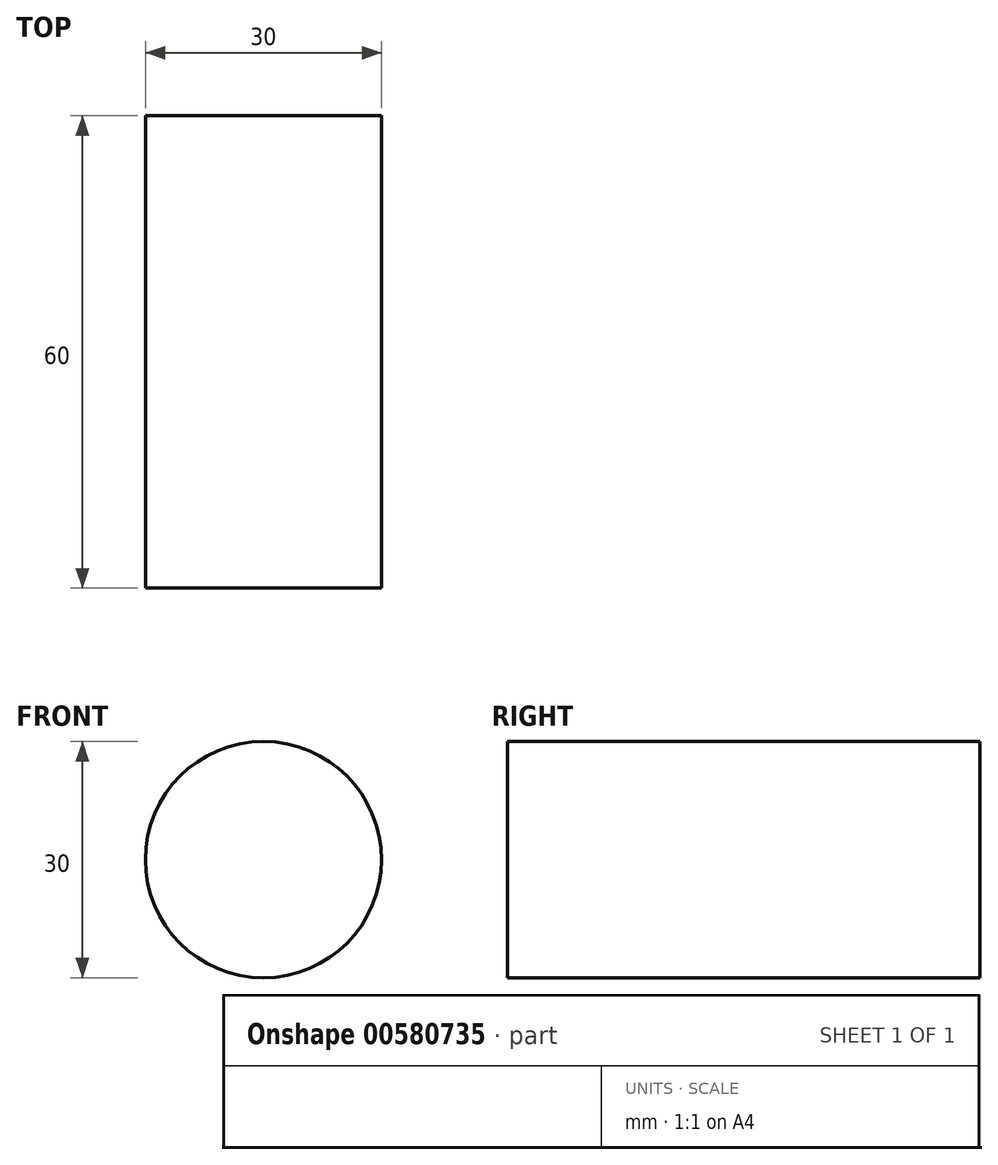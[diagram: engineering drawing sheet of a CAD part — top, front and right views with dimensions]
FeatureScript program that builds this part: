
annotation { "Feature Type Name" : "Feature", "Feature Type Description" : "" }
export const myFeature = defineFeature(function(context is Context, id is Id, definition is map)
    precondition{}
    {
        {
            var Q0;
            Q0=qCreatedBy(makeId("Front.planeOp"),FACE);
            var sketch = newSketch(context, id + "F0", { "sketchPlane" : qUnion([Q0])});
            skCircle(sketch, "E0", {"center": v(0, 0) * mm, "radius": 15 * mm});
            skSolve(sketch);
        }
        {
            var Q0;
            Q0 = qSketchRegion(id + "F0", true);
            extrude(context, id + "F1", {"entities" : qUnion([Q0]), "depth" : 60 * mm, "offsetDistance" : 25 * mm});
        }
    });
